# Revit family: Mixing_Valve-Sink_Faucet-Bradley_Corp-Navigator_TMV-S59-4000BY
name_source: partatom
category: Pipe Accessories
revit_build: Autodesk Revit MEP 2012 (Build: 20110309_2315(x64)
units: mm (PartAtom-declared; Revit-internal decimal feet)

## types (1)
- Navigator
    ADA Compliant = No
    Assembly Code = D2090800
    Buy American Act = To Be Determined
    Cap Material = Plastic - Bradley Corp - Gray
    Description = Point of Use Thermostatic Mixing Valve
    Fittings Material = Brass - Bradley Corp - Lead-Free Brass
    Industry Standards = ASSE 1070, cUPC. Certified by IAPMO to meet the lead-free requirements of CA AB 1953.
    Manufacturer = Bradley Corporation
    MasterFormat Number = 22 40 00
    MasterFormat Title = Plumbing Fixtures
    Material = Lead-free Brass
    Maximum Inlet Temperature = 180°F (82°C)
    Maximum Operating Pressure = 125.00 psi
    Minimum Flow = 0.500 GPM
    Model = S59-4000BY
    NPT = 0"
    NPT Radius = 0"
    OmniClass Code = 23.65.55.14.24
    OmniClass Title = Mixing Valves for Liquid Services
    Product Tech Data URL - English = http://bradleycorp.com
    Specifications URL = http://www.bradleycorp.com
    Temperature Differential - Hot to Mix = 10°F (18°C)
    Temperature Range = 95°F (35°C) to 125°F (52°C)
    URL = http://www.bradleycorp.com
    Valve Body Material = Plastic - Bradley Corp - Black
    Version = 2.0

## geometry (parser evidence)
native form markers: Blend x2, Sweep x4
no freeform markers — native parametric forms only
